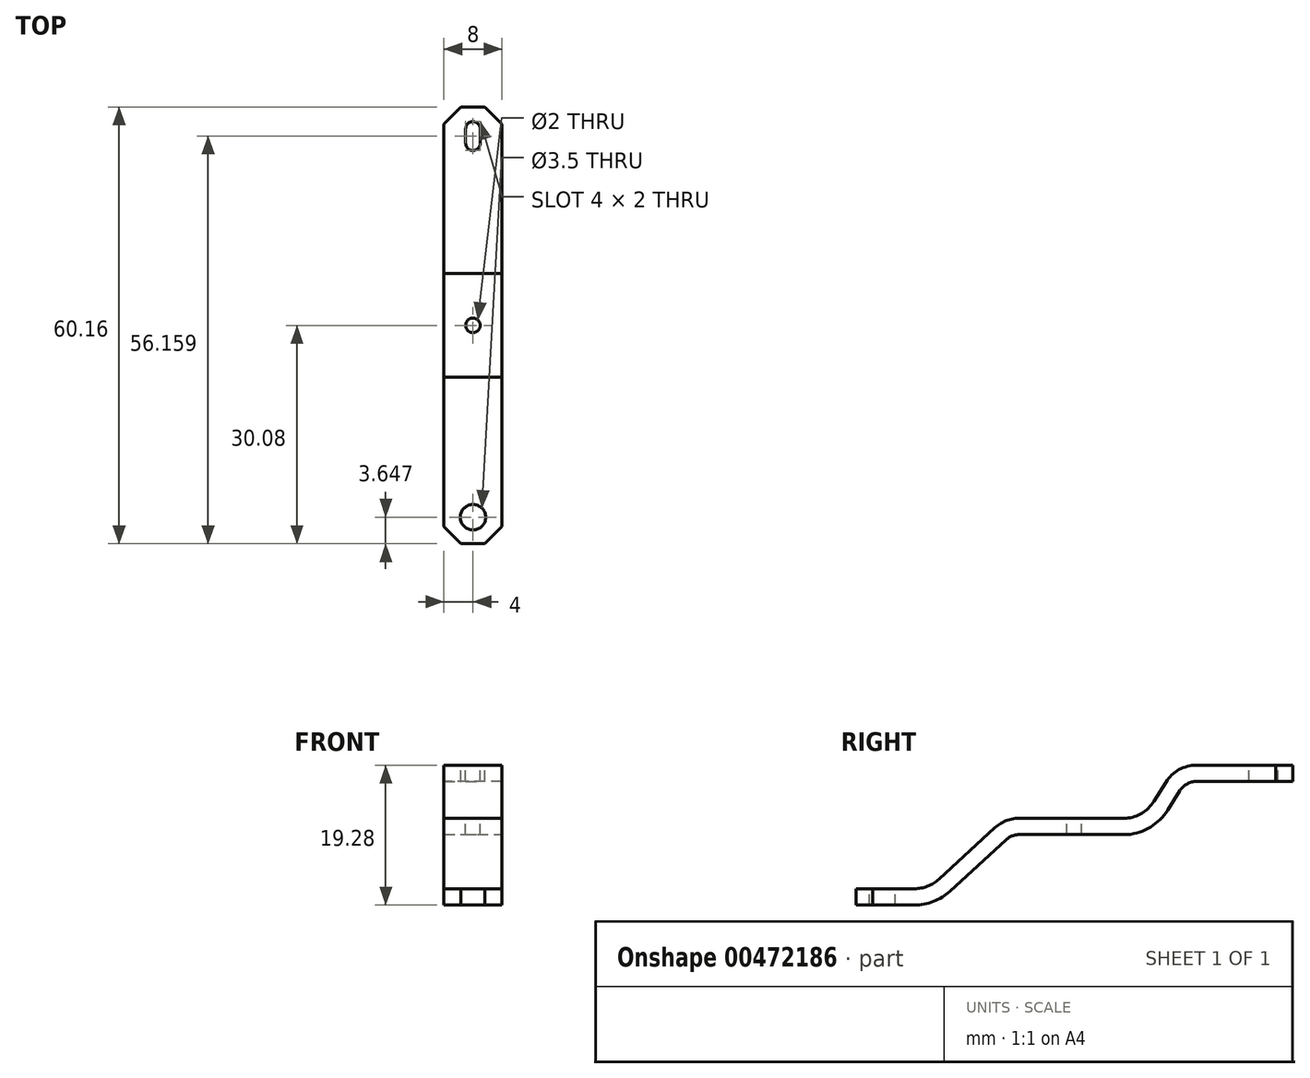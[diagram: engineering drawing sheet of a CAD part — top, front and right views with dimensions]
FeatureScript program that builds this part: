
annotation { "Feature Type Name" : "Feature", "Feature Type Description" : "" }
export const myFeature = defineFeature(function(context is Context, id is Id, definition is map)
    precondition{}
    {
        {
            var Q0;
            Q0=qCreatedBy(makeId("Right.planeOp"),FACE);
            var sketch = newSketch(context, id + "F0", { "sketchPlane" : qUnion([Q0])});
            skPoint(sketch, "E0", {"position": v(0, 0) * mm});
            skLineSegment(sketch, "E1", {"start": v(10.96, 2.33) * mm, "end": v(12.61, 4.98) * mm});
            skLineSegment(sketch, "E2", {"start": v(16.85, 7.33) * mm, "end": v(30.08, 7.33) * mm});
            skPoint(sketch, "E3.visualSharp", {"position": v(14.08, 7.33) * mm});
            skArc(sketch, "E3.filletArc", {"start": v(16.85, 7.32) * mm, "mid": v(14.43, 6.7) * mm, "end": v(12.61, 4.98) * mm});
            skPoint(sketch, "E4.visualSharp", {"position": v(9.5, 0) * mm});
            skArc(sketch, "E4.filletArc", {"start": v(7.14, 0) * mm, "mid": v(9.32, 0.72) * mm, "end": v(10.96, 2.33) * mm});
            skLineSegment(sketch, "E5", {"start": v(-10.92, -1.3) * mm, "end": v(-18.65, -8.39) * mm});
            skLineSegment(sketch, "E6", {"start": v(-22.02, -9.7) * mm, "end": v(-30.08, -9.7) * mm});
            skLineSegment(sketch, "E7", {"start": v(-30.08, -9.7) * mm, "end": v(30.08, -9.7) * mm, "construction": true});
            skPoint(sketch, "E8", {"position": v(0, -9.7) * mm});
            skPoint(sketch, "E9.visualSharp", {"position": v(-9.5, 0) * mm});
            skArc(sketch, "E9.filletArc", {"start": v(-7.14, 0) * mm, "mid": v(-9.16, -0.26) * mm, "end": v(-10.92, -1.3) * mm});
            skPoint(sketch, "E10.visualSharp", {"position": v(-20.08, -9.7) * mm});
            skArc(sketch, "E10.filletArc", {"start": v(-22.02, -9.7) * mm, "mid": v(-20.21, -9.36) * mm, "end": v(-18.65, -8.39) * mm});
            skLineSegment(sketch, "E11", {"start": v(7.14, 0) * mm, "end": v(-7.14, 0) * mm});
            skSolve(sketch);
        }
        {
            var Q0;
            Q0=qCreatedBy(makeId("Front.planeOp"),FACE);
            var Q1;
            Q1=sQuery(id+"F0.wireOp",VERTEX,"E2.end");
            cPlane(context, id + "F1", {"entities" : qUnion([Q0, Q1]), "cplaneType" : CPlaneType.PLANE_POINT, "offset" : 25 * mm, "width" : 150 * mm, "height" : 150 * mm});
        }
        {
            var Q0;
            Q0=qCreatedBy(id+"F1.planeOp",FACE);
            var sketch = newSketch(context, id + "F2", { "sketchPlane" : qUnion([Q0])});
            skLineSegment(sketch, "E12.bottom", {"start": v(4, 7.33) * mm, "end": v(-4, 7.33) * mm});
            skLineSegment(sketch, "E12.top", {"start": v(4, 5.08) * mm, "end": v(-4, 5.08) * mm});
            skLineSegment(sketch, "E12.left", {"start": v(-4, 7.33) * mm, "end": v(-4, 5.08) * mm});
            skLineSegment(sketch, "E12.right", {"start": v(4, 7.33) * mm, "end": v(4, 5.08) * mm});
            skSolve(sketch);
        }
        {
            var Q0;
            Q0 = qSketchRegion(id + "F2", true);
            var Q1;
            Q1 = qConstructionFilter(qBodyType(qCreatedBy(id + "F0" ,EDGE), BodyType.WIRE), ConstructionObject.NO);
            sweep(context, id + "F3", {"profiles" : qUnion([Q0]), "path" : qUnion([Q1])});
        }
        {
            var Q0;
            Q0=makeQuery(id+"F3.opSweep","SWEPT_FACE",FACE,{"disambiguationData":[OSD([sQuery(id+"F0.wireOp",EDGE,"E2"),sQuery(id+"F2.wireOp",EDGE,"E12.bottom")])]});
            var sketch = newSketch(context, id + "F4", { "sketchPlane" : qUnion([Q0])});
            skCircle(sketch, "E13", {"center": v(0, 0) * mm, "radius": 1 * mm});
            skLineSegment(sketch, "E14", {"start": v(0, 27.08) * mm, "end": v(0, 25.08) * mm, "construction": true});
            skPoint(sketch, "E15", {"position": v(0, 26.08) * mm});
            skArc(sketch, "E16.0.startCap", {"start": v(-1, 27.08) * mm, "mid": v(0, 28.08) * mm, "end": v(1, 27.08) * mm});
            skArc(sketch, "E16.0.endCap", {"start": v(1, 25.08) * mm, "mid": v(0, 24.08) * mm, "end": v(-1, 25.08) * mm});
            skLineSegment(sketch, "E16.0.left", {"start": v(1, 27.08) * mm, "end": v(1, 25.08) * mm});
            skLineSegment(sketch, "E16.0.right", {"start": v(-1, 27.08) * mm, "end": v(-1, 25.08) * mm});
            skCircle(sketch, "E17", {"center": v(0, -26.43) * mm, "radius": 1.75 * mm});
            skLineSegment(sketch, "E18.0", {"start": v(4, -27.74) * mm, "end": v(4, -30.08) * mm});
            skLineSegment(sketch, "E19.0", {"start": v(-4, -27.74) * mm, "end": v(-4, -30.08) * mm});
            skLineSegment(sketch, "E20.0", {"start": v(4, -30.08) * mm, "end": v(-4, -30.08) * mm});
            skLineSegment(sketch, "E21", {"start": v(-1.66, -30.08) * mm, "end": v(-4, -27.74) * mm});
            skLineSegment(sketch, "E22.MirrorCS", {"start": v(1.66, -30.08) * mm, "end": v(4, -27.74) * mm});
            skLineSegment(sketch, "E23", {"start": v(1.66, -30.08) * mm, "end": v(-1.66, -30.08) * mm});
            skPoint(sketch, "E24.orphan", {"position": v(4, -22.02) * mm});
            skPoint(sketch, "E25.orphan", {"position": v(-4, -22.02) * mm});
            skLineSegment(sketch, "E26.MirrorCS", {"start": v(-1.66, 30.08) * mm, "end": v(-4, 27.74) * mm});
            skLineSegment(sketch, "E27.MirrorCS", {"start": v(-4, 27.74) * mm, "end": v(-4, 30.08) * mm});
            skLineSegment(sketch, "E28.MirrorCS", {"start": v(4, 30.08) * mm, "end": v(-4, 30.08) * mm});
            skLineSegment(sketch, "E29.MirrorCS", {"start": v(4, 27.74) * mm, "end": v(4, 30.08) * mm});
            skLineSegment(sketch, "E30.MirrorCS", {"start": v(1.66, 30.08) * mm, "end": v(-1.66, 30.08) * mm});
            skLineSegment(sketch, "E31.MirrorCS", {"start": v(1.66, 30.08) * mm, "end": v(4, 27.74) * mm});
            skSolve(sketch);
        }
        {
            var Q0;
            Q0 = qSketchRegion(id + "F4", true);
            var Q1;
            Q1=makeQuery(id+"F3.opSweep","SWEPT_FACE",FACE,{"disambiguationData":[OSD([sQuery(id+"F0.wireOp",EDGE,"E6"),sQuery(id+"F2.wireOp",EDGE,"E12.top")])]});
            extrude(context, id + "F5", {"entities" : qUnion([Q0]), "operationType" : NewBodyOperationType.REMOVE, "endBound" : BoundingType.UP_TO_SURFACE, "oppositeDirection" : true, "endBoundEntityFace" : qUnion([Q1]), "depth" : 25 * mm});
        }
    });
